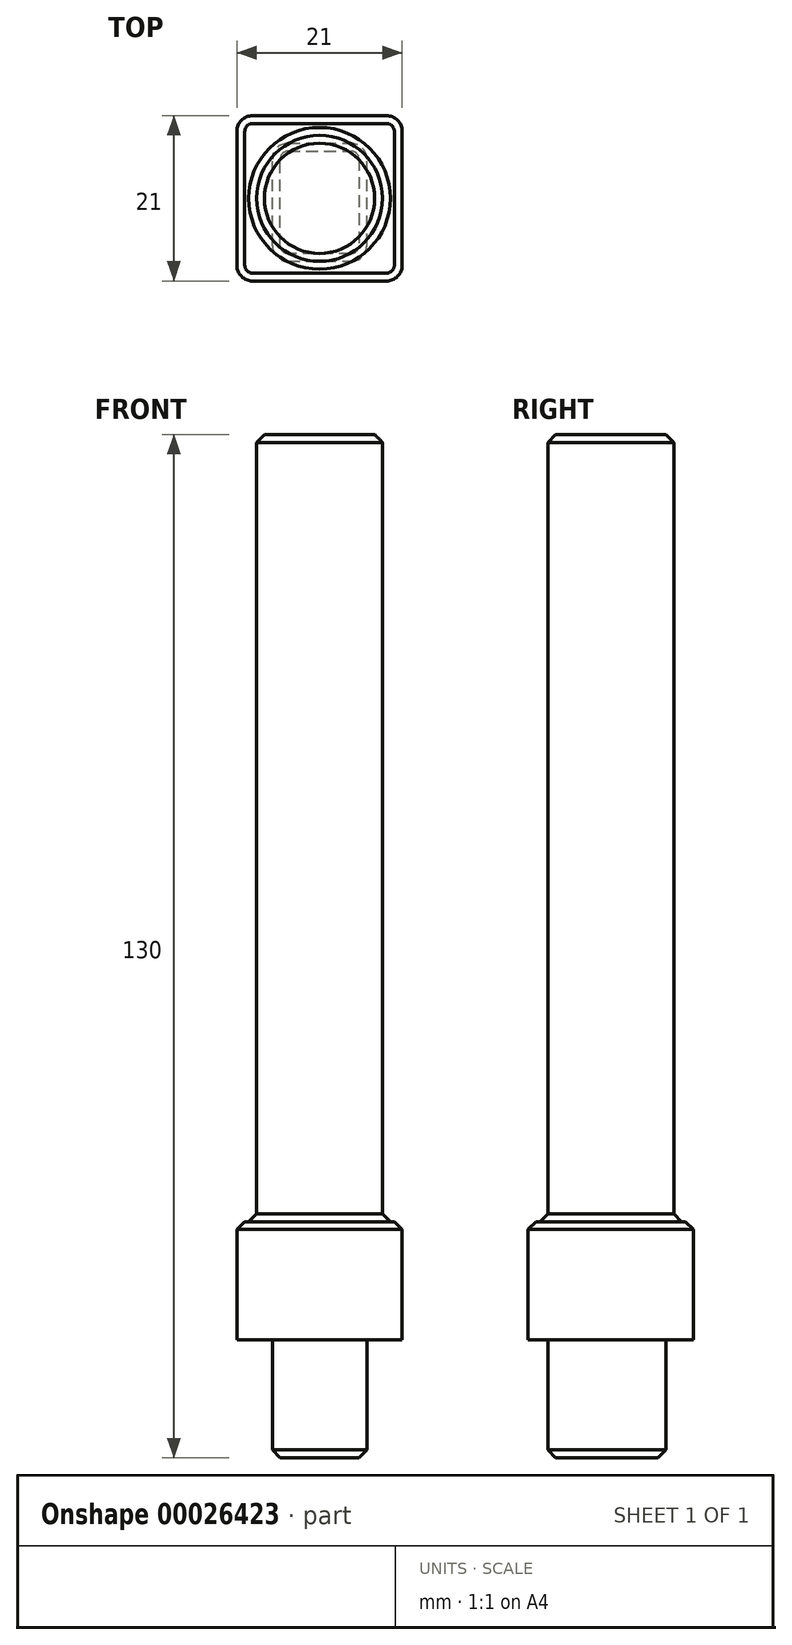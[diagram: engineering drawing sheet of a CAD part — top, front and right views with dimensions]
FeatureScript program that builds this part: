
annotation { "Feature Type Name" : "Feature", "Feature Type Description" : "" }
export const myFeature = defineFeature(function(context is Context, id is Id, definition is map)
    precondition{}
    {
        {
            var Q0;
            Q0=qCreatedBy(makeId("Top.planeOp"),FACE);
            var sketch = newSketch(context, id + "F0", { "sketchPlane" : qUnion([Q0])});
            skLineSegment(sketch, "E0.bottom", {"start": v(-8.5, 10.5) * mm, "end": v(8.5, 10.5) * mm});
            skLineSegment(sketch, "E0.top", {"start": v(-8.5, -10.5) * mm, "end": v(8.5, -10.5) * mm});
            skLineSegment(sketch, "E0.left", {"start": v(-10.5, 8.5) * mm, "end": v(-10.5, -8.5) * mm});
            skLineSegment(sketch, "E0.right", {"start": v(10.5, 8.5) * mm, "end": v(10.5, -8.5) * mm});
            skLineSegment(sketch, "E1", {"start": v(0, 10.5) * mm, "end": v(0, -10.5) * mm, "construction": true});
            skPoint(sketch, "E2.visualSharp", {"position": v(-10.5, 10.5) * mm});
            skArc(sketch, "E2.filletArc", {"start": v(-8.5, 10.5) * mm, "mid": v(-9.91, 9.91) * mm, "end": v(-10.5, 8.5) * mm});
            skPoint(sketch, "E3.visualSharp", {"position": v(-10.5, -10.5) * mm});
            skArc(sketch, "E3.filletArc", {"start": v(-10.5, -8.5) * mm, "mid": v(-9.91, -9.91) * mm, "end": v(-8.5, -10.5) * mm});
            skPoint(sketch, "E4.visualSharp", {"position": v(10.5, -10.5) * mm});
            skArc(sketch, "E4.filletArc", {"start": v(8.5, -10.5) * mm, "mid": v(9.91, -9.91) * mm, "end": v(10.5, -8.5) * mm});
            skPoint(sketch, "E5.visualSharp", {"position": v(10.5, 10.5) * mm});
            skArc(sketch, "E5.filletArc", {"start": v(10.5, 8.5) * mm, "mid": v(9.91, 9.91) * mm, "end": v(8.5, 10.5) * mm});
            skSolve(sketch);
        }
        {
            var Q0;
            Q0 = qSketchRegion(id + "F0", true);
            extrude(context, id + "F1", {"entities" : qUnion([Q0]), "depth" : 15 * mm});
        }
        {
            var Q0;
            Q0=makeQuery(id+"F1.opExtrude","CAP_FACE",FACE,{"disambiguationData":[OSD([sQuery(id+"F0.wireOp",EDGE,"E0.bottom"),sQuery(id+"F0.wireOp",EDGE,"E0.top"),sQuery(id+"F0.wireOp",EDGE,"E0.left"),sQuery(id+"F0.wireOp",EDGE,"E0.right"),sQuery(id+"F0.wireOp",EDGE,"E2.filletArc"),sQuery(id+"F0.wireOp",EDGE,"E3.filletArc"),sQuery(id+"F0.wireOp",EDGE,"E4.filletArc"),sQuery(id+"F0.wireOp",EDGE,"E5.filletArc")])],"isStart":true});
            var sketch = newSketch(context, id + "F2", { "sketchPlane" : qUnion([Q0])});
            skLineSegment(sketch, "E6.bottom", {"start": v(-4, 8) * mm, "end": v(4, 8) * mm});
            skLineSegment(sketch, "E6.top", {"start": v(-4, -7) * mm, "end": v(4, -7) * mm});
            skLineSegment(sketch, "E6.left", {"start": v(-6, 6) * mm, "end": v(-6, -5) * mm});
            skLineSegment(sketch, "E6.right", {"start": v(6, 6) * mm, "end": v(6, -5) * mm});
            skLineSegment(sketch, "E7", {"start": v(0, 10.5) * mm, "end": v(0, 8) * mm, "construction": true});
            skPoint(sketch, "E8.visualSharp", {"position": v(-6, 8) * mm});
            skArc(sketch, "E8.filletArc", {"start": v(-4, 8) * mm, "mid": v(-5.41, 7.41) * mm, "end": v(-6, 6) * mm});
            skPoint(sketch, "E9.visualSharp", {"position": v(6, 8) * mm});
            skArc(sketch, "E9.filletArc", {"start": v(6, 6) * mm, "mid": v(5.41, 7.41) * mm, "end": v(4, 8) * mm});
            skPoint(sketch, "E10.visualSharp", {"position": v(6, -7) * mm});
            skArc(sketch, "E10.filletArc", {"start": v(4, -7) * mm, "mid": v(5.41, -6.41) * mm, "end": v(6, -5) * mm});
            skPoint(sketch, "E11.visualSharp", {"position": v(-6, -7) * mm});
            skArc(sketch, "E11.filletArc", {"start": v(-6, -5) * mm, "mid": v(-5.41, -6.41) * mm, "end": v(-4, -7) * mm});
            skSolve(sketch);
        }
        {
            var Q0;
            Q0 = qSketchRegion(id + "F2", true);
            extrude(context, id + "F3", {"entities" : qUnion([Q0]), "operationType" : NewBodyOperationType.ADD, "depth" : 15 * mm});
        }
        {
            var Q0;
            Q0=makeQuery(id+"F3.opExtrude","CAP_FACE",FACE,{"disambiguationData":[OSD([sQuery(id+"F2.wireOp",EDGE,"E6.bottom"),sQuery(id+"F2.wireOp",EDGE,"E6.top"),sQuery(id+"F2.wireOp",EDGE,"E6.left"),sQuery(id+"F2.wireOp",EDGE,"E6.right"),sQuery(id+"F2.wireOp",EDGE,"E8.filletArc"),sQuery(id+"F2.wireOp",EDGE,"E9.filletArc"),sQuery(id+"F2.wireOp",EDGE,"E10.filletArc"),sQuery(id+"F2.wireOp",EDGE,"E11.filletArc")])],"isStart":false});
            var Q1;
            Q1=makeQuery(id+"F1.opExtrude","CAP_FACE",FACE,{"disambiguationData":[OSD([sQuery(id+"F0.wireOp",EDGE,"E0.bottom"),sQuery(id+"F0.wireOp",EDGE,"E0.top"),sQuery(id+"F0.wireOp",EDGE,"E0.left"),sQuery(id+"F0.wireOp",EDGE,"E0.right"),sQuery(id+"F0.wireOp",EDGE,"E2.filletArc"),sQuery(id+"F0.wireOp",EDGE,"E3.filletArc"),sQuery(id+"F0.wireOp",EDGE,"E4.filletArc"),sQuery(id+"F0.wireOp",EDGE,"E5.filletArc")])],"isStart":false});
            chamfer(context, id + "F4", {"entities" : qUnion([Q0, Q1]), "width" : 1 * mm, "tangentPropagation" : true});
        }
        {
            var Q0;
            Q0=makeQuery(id+"F1.opExtrude","CAP_FACE",FACE,{"disambiguationData":[OSD([sQuery(id+"F0.wireOp",EDGE,"E0.bottom"),sQuery(id+"F0.wireOp",EDGE,"E0.top"),sQuery(id+"F0.wireOp",EDGE,"E0.left"),sQuery(id+"F0.wireOp",EDGE,"E0.right"),sQuery(id+"F0.wireOp",EDGE,"E2.filletArc"),sQuery(id+"F0.wireOp",EDGE,"E3.filletArc"),sQuery(id+"F0.wireOp",EDGE,"E4.filletArc"),sQuery(id+"F0.wireOp",EDGE,"E5.filletArc")])],"isStart":false});
            var sketch = newSketch(context, id + "F5", { "sketchPlane" : qUnion([Q0])});
            skCircle(sketch, "E12", {"center": v(0, 0) * mm, "radius": 8 * mm});
            skSolve(sketch);
        }
        {
            var Q0;
            Q0 = qSketchRegion(id + "F5", true);
            extrude(context, id + "F6", {"entities" : qUnion([Q0]), "operationType" : NewBodyOperationType.ADD, "depth" : 100 * mm});
        }
        {
            var Q0;
            Q0=makeQuery(id+"F6.opExtrude","SWEPT_FACE",FACE,{"disambiguationData":[OSD([sQuery(id+"F5.wireOp",EDGE,"E12")])]});
            chamfer(context, id + "F7", {"entities" : qUnion([Q0]), "width" : 1 * mm, "tangentPropagation" : true});
        }
    });
